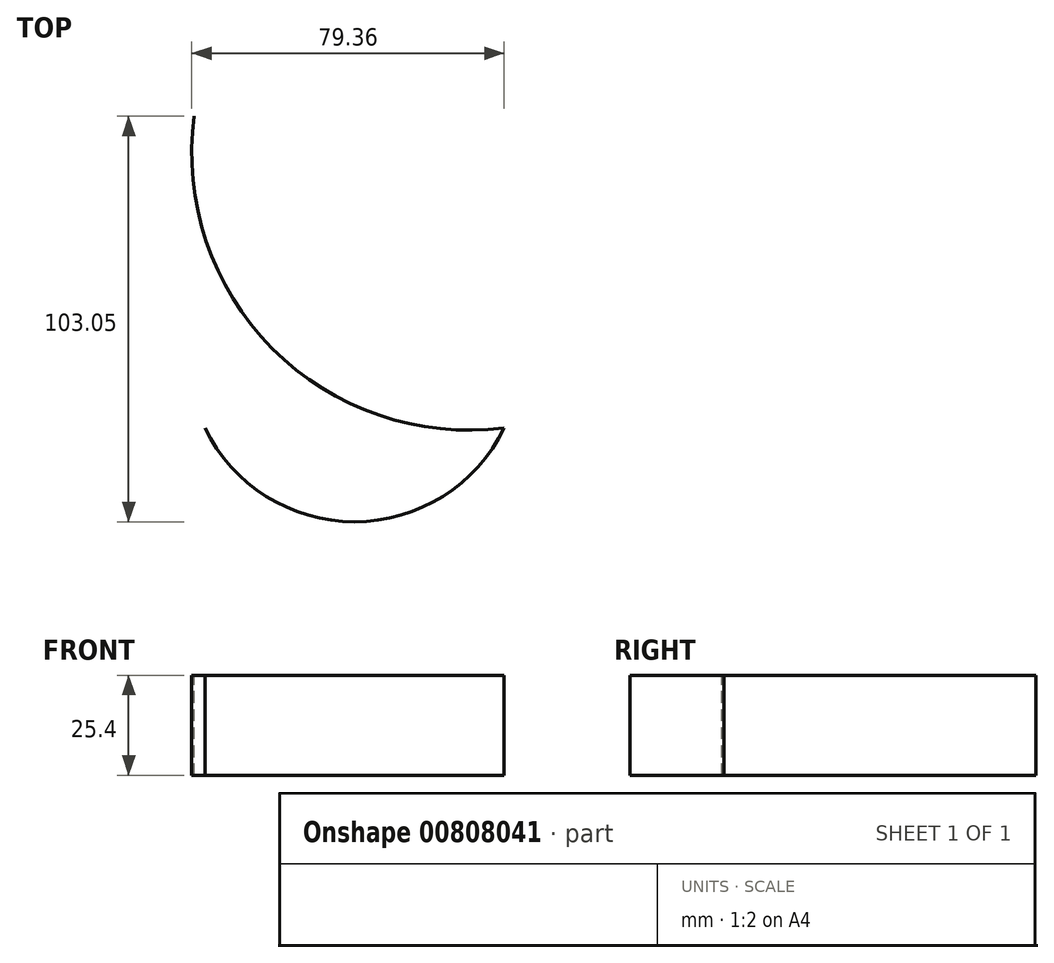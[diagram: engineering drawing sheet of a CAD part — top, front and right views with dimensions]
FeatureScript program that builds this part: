
annotation { "Feature Type Name" : "Feature", "Feature Type Description" : "" }
export const myFeature = defineFeature(function(context is Context, id is Id, definition is map)
    precondition{}
    {
        {
            var Q0;
            Q0=qCreatedBy(makeId("Top.planeOp"),FACE);
            var sketch = newSketch(context, id + "F0", { "sketchPlane" : qUnion([Q0])});
            skArc(sketch, "E0", {"start": v(0, -74.52) * mm, "mid": v(22.43, -37.26) * mm, "end": v(0, 0) * mm});
            skArc(sketch, "E1", {"start": v(-75.99, 0) * mm, "mid": v(-38, -23.88) * mm, "end": v(0, 0) * mm});
            skArc(sketch, "E2", {"start": v(0, 73.6) * mm, "mid": v(-21.58, 36.8) * mm, "end": v(0, 0) * mm});
            skArc(sketch, "E3", {"start": v(73.82, 0) * mm, "mid": v(36.91, 21.78) * mm, "end": v(0, 0) * mm});
            skArc(sketch, "E4", {"start": v(-76.49, -76.93) * mm, "mid": v(-20.13, -56.48) * mm, "end": v(0, 0) * mm});
            skArc(sketch, "E5", {"start": v(74.86, -75.57) * mm, "mid": v(54.7, -20.68) * mm, "end": v(0, 0) * mm});
            skArc(sketch, "E6", {"start": v(71.33, 70.93) * mm, "mid": v(20.75, 50.47) * mm, "end": v(0, 0) * mm});
            skArc(sketch, "E7", {"start": v(-78.73, 79.17) * mm, "mid": v(-58.9, 20.17) * mm, "end": v(0, 0) * mm});
            skArc(sketch, "E8", {"start": v(-78.73, 79.17) * mm, "mid": v(-40.4, 61.7) * mm, "end": v(0, 73.6) * mm});
            skArc(sketch, "E9", {"start": v(71.33, 70.93) * mm, "mid": v(36.04, 82.22) * mm, "end": v(0, 73.6) * mm});
            skArc(sketch, "E10", {"start": v(71.33, 70.93) * mm, "mid": v(64.67, 35.19) * mm, "end": v(73.82, 0) * mm});
            skArc(sketch, "E11", {"start": v(74.86, -75.57) * mm, "mid": v(82.15, -37.68) * mm, "end": v(73.82, 0) * mm});
            skArc(sketch, "E12", {"start": v(74.86, -75.57) * mm, "mid": v(37.57, -65) * mm, "end": v(0, -74.52) * mm});
            skArc(sketch, "E13", {"start": v(-76.49, -76.93) * mm, "mid": v(-38, -83.34) * mm, "end": v(0, -74.52) * mm});
            skArc(sketch, "E14", {"start": v(-76.49, -76.93) * mm, "mid": v(-66.75, -38.53) * mm, "end": v(-75.99, 0) * mm});
            skArc(sketch, "E15", {"start": v(-78.73, 79.17) * mm, "mid": v(-88.27, 39.2) * mm, "end": v(-75.99, 0) * mm});
            skSolve(sketch);
        }
        {
            var Q0;
            {var subQ0=sQuery(id+"F0.wireOp",EDGE,"E7");Q0=makeQuery(id+"F0.imprint","IMPRINT",FACE,{"disambiguationData":[TD([[makeQuery(id+"F0.imprint","IMPRINT",EDGE,{"derivedFrom":subQ0}),1.0]])]});}
            var Q1;
            Q1=makeQuery(id+"F0.imprint","IMPRINT",FACE,{"disambiguationData":[TD([[makeQuery(id+"F0.imprint","IMPRINT",EDGE,{"derivedFrom":sQuery(id+"F0.wireOp",EDGE,"E3")}),-1.0]])]});
            var Q2;
            {var subQ0=sQuery(id+"F0.wireOp",EDGE,"E5");Q2=makeQuery(id+"F0.imprint","IMPRINT",FACE,{"disambiguationData":[TD([[makeQuery(id+"F0.imprint","IMPRINT",EDGE,{"derivedFrom":subQ0}),1.0]])]});}
            var Q3;
            {var subQ0=sQuery(id+"F0.wireOp",EDGE,"E4");Q3=makeQuery(id+"F0.imprint","IMPRINT",FACE,{"disambiguationData":[TD([[makeQuery(id+"F0.imprint","IMPRINT",EDGE,{"derivedFrom":subQ0}),1.0]])]});}
            var Q4;
            Q4=sQuery(id+"F0.wireOp",EDGE,"E7");
            var Q5;
            Q5=sQuery(id+"F0.wireOp",EDGE,"E1");
            extrude(context, id + "F1", {"entities" : qUnion([Q0, Q1, Q2, Q3]), "bodyType" : ToolBodyType.SURFACE, "surfaceEntities" : qUnion([Q4, Q5]), "depth" : 25.4 * mm, "offsetDistance" : 25.4 * mm});
        }
    });
